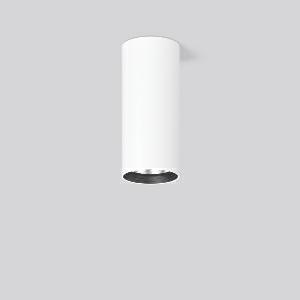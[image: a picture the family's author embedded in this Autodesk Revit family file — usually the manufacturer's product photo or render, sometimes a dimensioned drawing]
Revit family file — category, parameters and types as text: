
# Revit family: heledon_mini_a_931202_002_3_76_c32e
name_source: partatom
category: Lighting Fixtures
units: mm (PartAtom-declared; Revit-internal decimal feet)

## family parameters
Cut with Voids When Loaded = No
Host = Face
Light Source = No
Part Type = Normal
Room Calculation Point = No
Round Connector Dimension = Use Diameter
Shared = No

## types (1)
- HELEDON mini A (1 x LED Modul 935, 2650 lm, 3500)
    Apparent Load = 20 VA
    Approval mark = CE
    CIE Flux Codes = 95 99 100 100 100
    Color Rendering = 92
    Color Temperature = 3500
    Default Elevation = 1800 mm
    Description = Series: HELEDON mini
Cylindrical surface-mounted downlight. Housing: die-cast aluminium, powder-coated. Internal ceiling frame polycarbonate with bayonet mounting. Black plastic ring and recessed LED to prevent glare from the side. Optical assembly with reflector made of MIRO-Silver with 98% total light reflection for outstanding efficiency - can be changed without tools. Best colour rendering index Ra>90. Suitable for Ceiling mounting. Easy installation with a separate ceiling frame with bayonet mounting and plug connection. Driver integrated. Connected via plug-in connector. High quality converter without flickering and stroboscopic effect. The following accessories can be mounted without use of tools: interchangeable lenses, decorative glasses, honeycomb louvre, clear and frosted diffusers, white interchangeable plastic ring. 
Colour: traffic white, matt (RAL 9016)
Diameter: 87 mm
Height: 197 mm
Lamp: LED
Socket: without socket
Colour temperature: 3500K
Colour rendering index (CRI): 92
System power: 20 W
Rated luminous flux: 2650 lm
Luminous efficiency: 133 lm/W
Control gear: Converter, dimmable, DALI
Protection class: I
Type of protection: IP 20
    Height = 197 mm
    Lamp = 1 x LED Modul 935
    Lamp Light Flux = 2650 lm
    Lamp count = 1
    Length = 87 mm
    Lifetime = 50000 h
    Luminous efficacy = 133 lm/W
    Manufacturer = RZB
    ModVariant = No
    Model = 931202.002.3.76
    Mounting Place = Ceiling
    Mounting Type = Surface mounted
    Number of Poles = 1
    OnlyDefault = Yes
    Power Factor = 1
    Product Name = HELEDON mini A
    Product group = Surface mounted downlights
    ProductGroupID = 302
    Protection Class = Protection class I
    Protection Degree = IP 20
    RLX_Detail_Level = 1
    RLX_Emergency_Light_Flux = 0 lm
    RLX_Emergency_Type = 0
    RLX_Emergency_Type_DB = No
    RlxData = <blob elided: 106085 chars, md5=75ade65c>
    Socket = socket
    Standby Power = 0 W
    System Light Flux = 2650 lm
    System Power = 20 W
    Type Comments = Product without accessories
    Type Image = 931188.002.jpg
    URL = http://relux.com
    VarID = ---
    Voltage = 230 V
    Voltage Range = 220-240 V
    Weight = 0.00 kg
    Width = 0 mm  [stored 0 ft]

note: [stored X ft] marks values corroborated as IEEE doubles in the binary element streams (Revit-internal decimal feet)

## geometry (parser evidence)
native form markers: Blend x4, Sweep x9
no freeform markers — native parametric forms only
